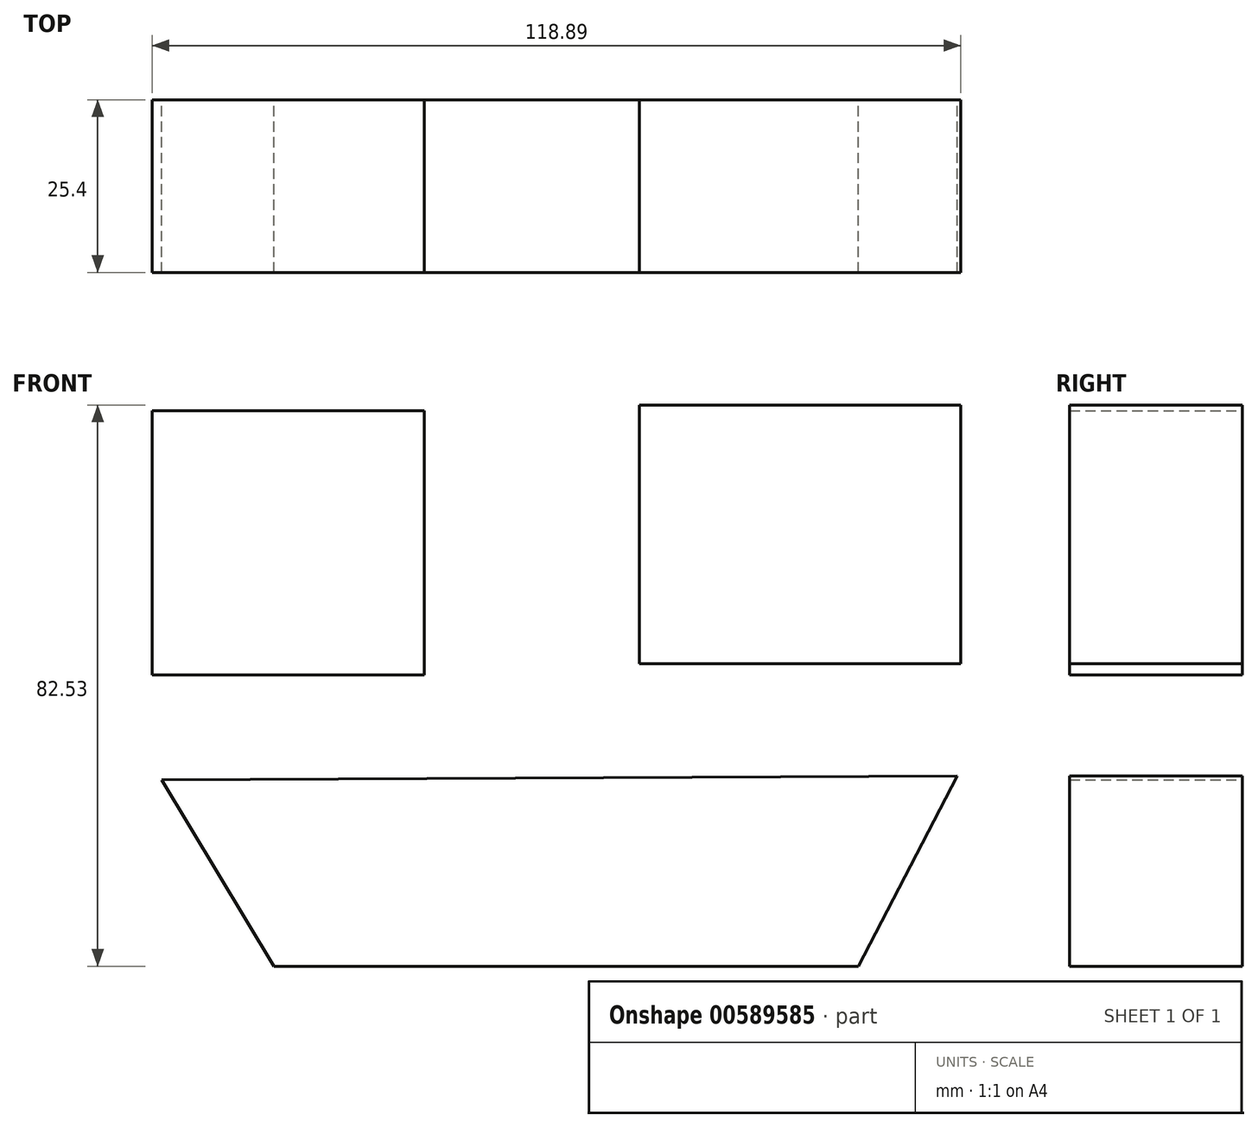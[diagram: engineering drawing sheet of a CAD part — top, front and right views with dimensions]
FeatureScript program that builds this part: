
annotation { "Feature Type Name" : "Feature", "Feature Type Description" : "" }
export const myFeature = defineFeature(function(context is Context, id is Id, definition is map)
    precondition{}
    {
        {
            var Q0;
            Q0=qCreatedBy(makeId("Front.planeOp"),FACE);
            var sketch = newSketch(context, id + "F0", { "sketchPlane" : qUnion([Q0])});
            skLineSegment(sketch, "E0.bottom", {"start": v(-55.53, 42.1) * mm, "end": v(-15.53, 42.1) * mm});
            skLineSegment(sketch, "E0.top", {"start": v(-55.53, 3.22) * mm, "end": v(-15.53, 3.22) * mm});
            skLineSegment(sketch, "E0.left", {"start": v(-55.53, 42.1) * mm, "end": v(-55.53, 3.22) * mm});
            skLineSegment(sketch, "E0.right", {"start": v(-15.53, 42.1) * mm, "end": v(-15.53, 3.22) * mm});
            skSolve(sketch);
        }
        {
            var Q0;
            Q0 = qSketchRegion(id + "F0", true);
            extrude(context, id + "F1", {"entities" : qUnion([Q0]), "depth" : 25.4 * mm, "offsetDistance" : 25.4 * mm});
        }
        {
            var Q0;
            Q0=qCreatedBy(makeId("Front.planeOp"),FACE);
            var sketch = newSketch(context, id + "F2", { "sketchPlane" : qUnion([Q0])});
            skLineSegment(sketch, "E1.bottom", {"start": v(16.09, 42.94) * mm, "end": v(63.36, 42.94) * mm});
            skLineSegment(sketch, "E1.top", {"start": v(16.09, 4.9) * mm, "end": v(63.36, 4.9) * mm});
            skLineSegment(sketch, "E1.left", {"start": v(16.09, 42.94) * mm, "end": v(16.09, 4.9) * mm});
            skLineSegment(sketch, "E1.right", {"start": v(63.36, 42.94) * mm, "end": v(63.36, 4.9) * mm});
            skSolve(sketch);
        }
        {
            var Q0;
            Q0 = qSketchRegion(id + "F2", true);
            extrude(context, id + "F3", {"entities" : qUnion([Q0]), "depth" : 25.4 * mm, "offsetDistance" : 25.4 * mm});
        }
        {
            var Q0;
            Q0=qCreatedBy(makeId("Front.planeOp"),FACE);
            var sketch = newSketch(context, id + "F4", { "sketchPlane" : qUnion([Q0])});
            skLineSegment(sketch, "E2", {"start": v(-54.13, -12.17) * mm, "end": v(-37.63, -39.59) * mm});
            skLineSegment(sketch, "E3", {"start": v(-37.63, -39.59) * mm, "end": v(-7.13, -39.59) * mm});
            skLineSegment(sketch, "E4", {"start": v(-7.13, -39.59) * mm, "end": v(37.63, -39.59) * mm});
            skLineSegment(sketch, "E5", {"start": v(37.63, -39.59) * mm, "end": v(48.26, -39.59) * mm});
            skLineSegment(sketch, "E6", {"start": v(48.26, -39.59) * mm, "end": v(62.8, -11.6) * mm});
            skLineSegment(sketch, "E7", {"start": v(-54.13, -12.17) * mm, "end": v(62.8, -11.6) * mm});
            skSolve(sketch);
        }
        {
            var Q0;
            Q0 = qSketchRegion(id + "F4", true);
            extrude(context, id + "F5", {"entities" : qUnion([Q0]), "depth" : 25.4 * mm, "offsetDistance" : 25.4 * mm});
        }
    });
